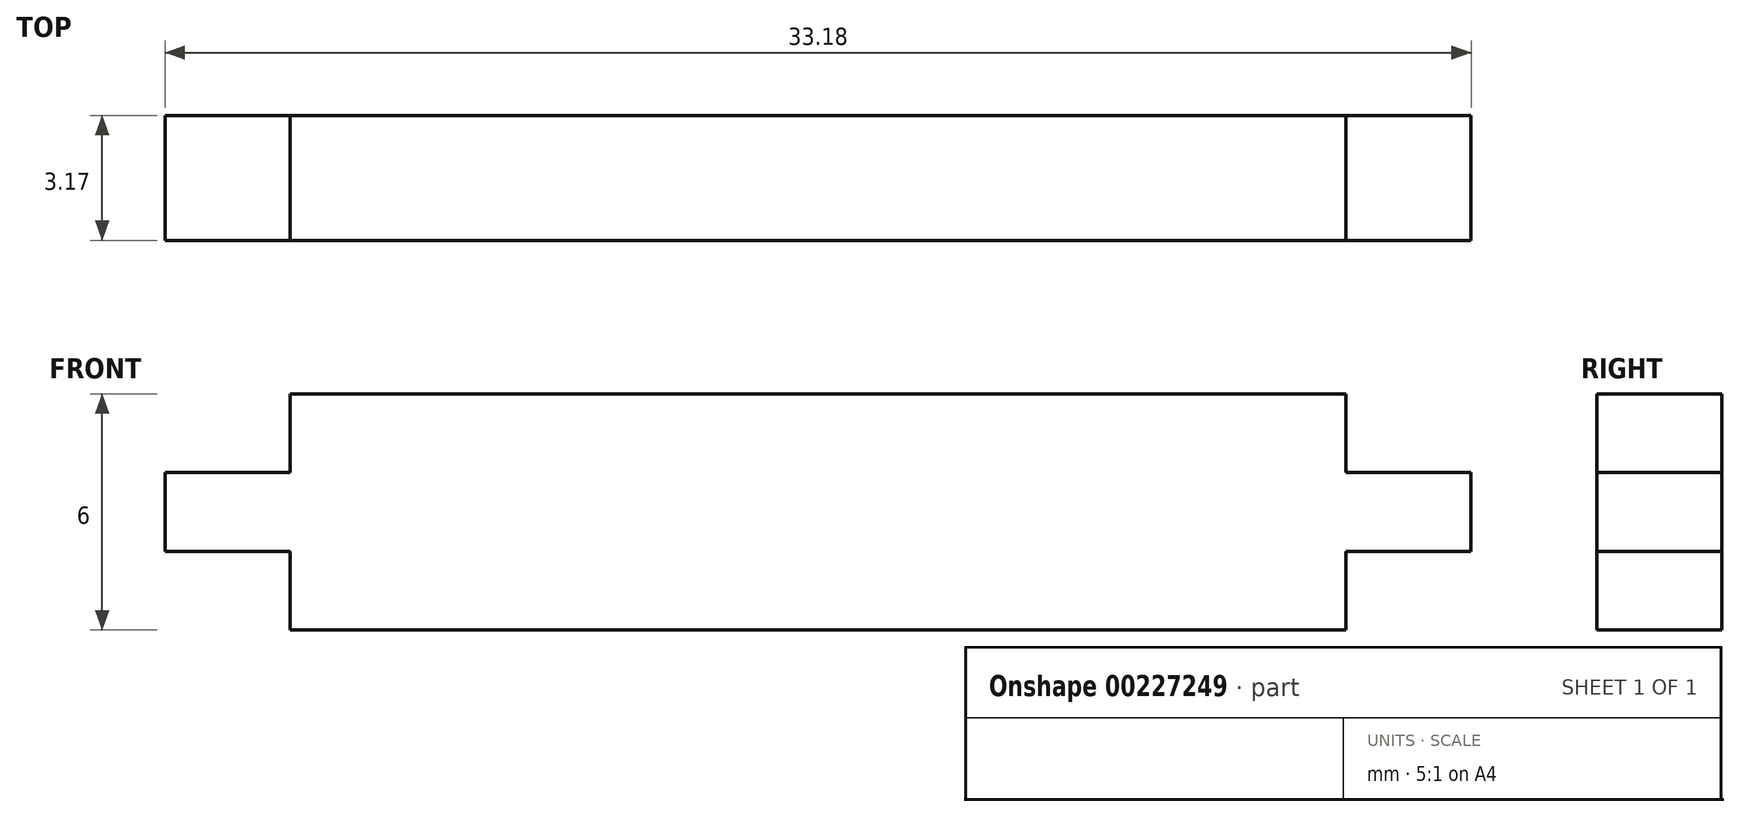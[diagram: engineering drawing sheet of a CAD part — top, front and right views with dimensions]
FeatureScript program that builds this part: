
annotation { "Feature Type Name" : "Feature", "Feature Type Description" : "" }
export const myFeature = defineFeature(function(context is Context, id is Id, definition is map)
    precondition{}
    {
        {
            var Q0;
            Q0=qCreatedBy(makeId("Front.planeOp"),FACE);
            var sketch = newSketch(context, id + "F0", { "sketchPlane" : qUnion([Q0])});
            skLineSegment(sketch, "E0.bottom", {"start": v(16.59, -1) * mm, "end": v(-16.59, -1) * mm});
            skLineSegment(sketch, "E0.top", {"start": v(16.59, 1) * mm, "end": v(-16.59, 1) * mm});
            skLineSegment(sketch, "E0.left", {"start": v(16.59, -1) * mm, "end": v(16.59, 1) * mm});
            skLineSegment(sketch, "E0.right", {"start": v(-16.59, -1) * mm, "end": v(-16.59, 1) * mm});
            skPoint(sketch, "E0.middle", {"position": v(0, 0) * mm});
            skLineSegment(sketch, "E1", {"start": v(-13.41, 1) * mm, "end": v(-13.41, 3) * mm});
            skLineSegment(sketch, "E2", {"start": v(-13.41, 3) * mm, "end": v(13.41, 3) * mm});
            skLineSegment(sketch, "E3", {"start": v(13.41, 3) * mm, "end": v(13.41, 1) * mm});
            skLineSegment(sketch, "E4.MirrorCS", {"start": v(-13.41, -3) * mm, "end": v(13.41, -3) * mm});
            skLineSegment(sketch, "E5.MirrorCS", {"start": v(-13.41, -1) * mm, "end": v(-13.41, -3) * mm});
            skLineSegment(sketch, "E6.MirrorCS", {"start": v(13.41, -3) * mm, "end": v(13.41, -1) * mm});
            skSolve(sketch);
        }
        {
            var Q0;
            Q0 = qSketchRegion(id + "F0", true);
            extrude(context, id + "F1", {"entities" : qUnion([Q0]), "depth" : 3.17 * mm});
        }
    });
